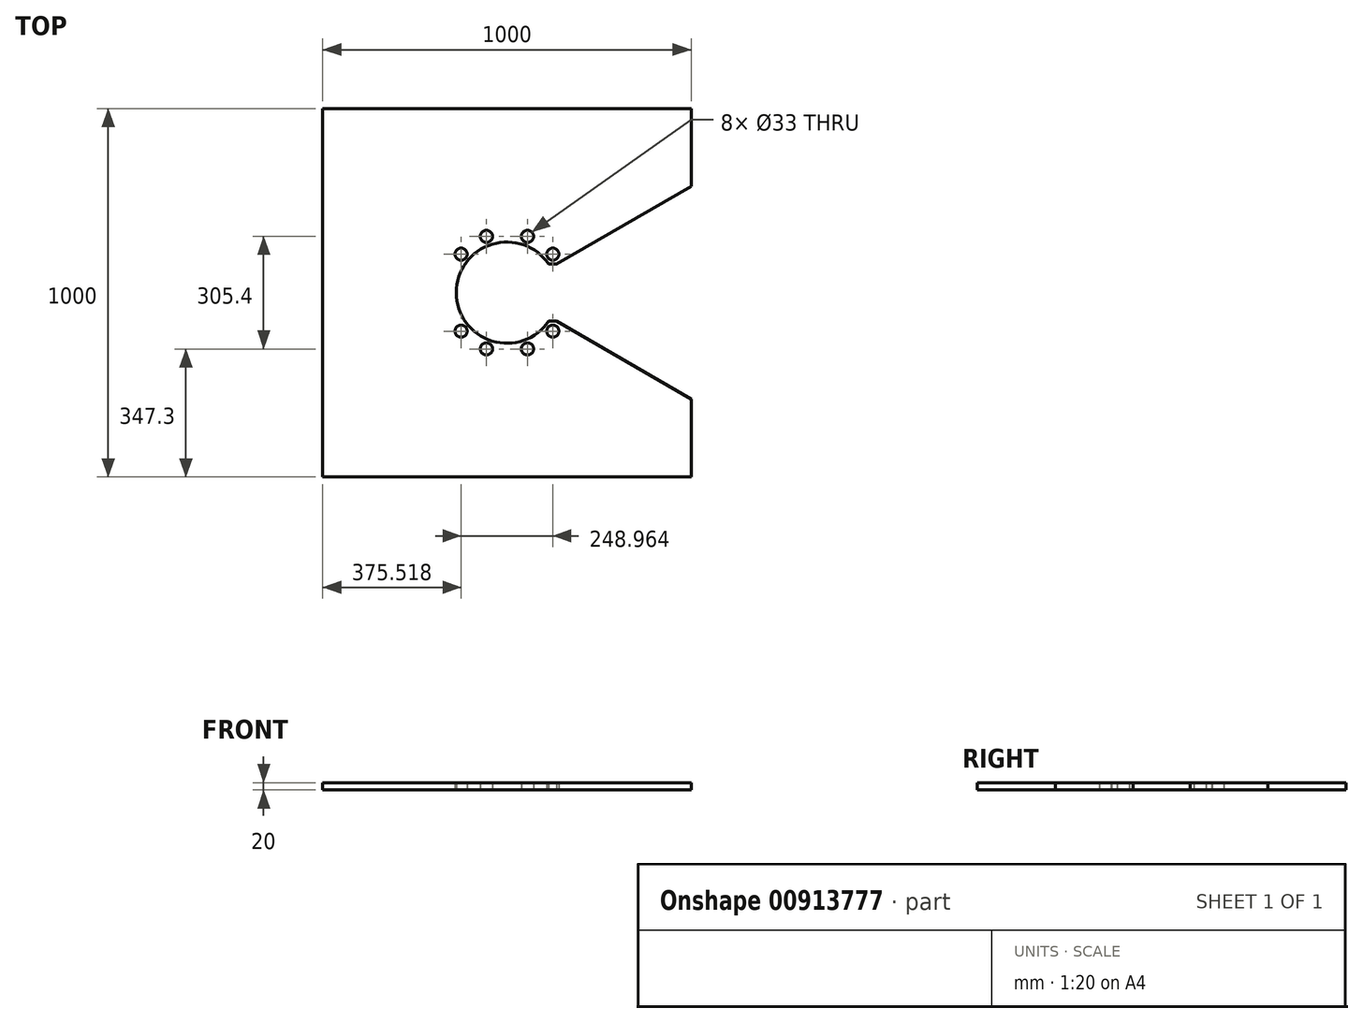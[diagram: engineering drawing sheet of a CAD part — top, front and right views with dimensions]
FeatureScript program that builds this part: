
annotation { "Feature Type Name" : "Feature", "Feature Type Description" : "" }
export const myFeature = defineFeature(function(context is Context, id is Id, definition is map)
    precondition{}
    {
        {
            var Q0;
            Q0=qCreatedBy(makeId("Top.planeOp"),FACE);
            var sketch = newSketch(context, id + "F0", { "sketchPlane" : qUnion([Q0])});
            skCircle(sketch, "E0", {"center": v(0, 0) * mm, "radius": 162.5 * mm, "construction": true});
            skLineSegment(sketch, "E1", {"start": v(0, 0) * mm, "end": v(72.3, 198.65) * mm, "construction": true});
            skCircle(sketch, "E2", {"center": v(55.58, 152.7) * mm, "radius": 16.5 * mm});
            skLineSegment(sketch, "E3", {"start": v(0, 0) * mm, "end": v(150.95, 126.66) * mm, "construction": true});
            skLineSegment(sketch, "E4", {"start": v(0, 0) * mm, "end": v(-63.14, 173.48) * mm, "construction": true});
            skLineSegment(sketch, "E5", {"start": v(0, 0) * mm, "end": v(-153.87, 129.1) * mm, "construction": true});
            skCircle(sketch, "E6", {"center": v(-55.58, 152.7) * mm, "radius": 16.5 * mm});
            skCircle(sketch, "E7", {"center": v(-124.48, 104.45) * mm, "radius": 16.5 * mm});
            skCircle(sketch, "E8", {"center": v(124.48, 104.45) * mm, "radius": 16.5 * mm});
            skCircle(sketch, "E9.MirrorC", {"center": v(-124.48, -104.45) * mm, "radius": 16.5 * mm});
            skCircle(sketch, "E10.MirrorC", {"center": v(-55.58, -152.7) * mm, "radius": 16.5 * mm});
            skCircle(sketch, "E11.MirrorC", {"center": v(55.58, -152.7) * mm, "radius": 16.5 * mm});
            skCircle(sketch, "E12.MirrorC", {"center": v(124.48, -104.45) * mm, "radius": 16.5 * mm});
            skArc(sketch, "E13", {"start": v(170.73, 77.5) * mm, "mid": v(-187.5, 0) * mm, "end": v(170.73, -77.5) * mm, "construction": true});
            skArc(sketch, "E14", {"start": v(113.58, 77.5) * mm, "mid": v(-137.5, 0) * mm, "end": v(113.58, -77.5) * mm});
            skCircle(sketch, "E15", {"center": v(0, 0) * mm, "radius": 77.5 * mm, "construction": true});
            skLineSegment(sketch, "E16.top", {"start": v(113.58, -77.5) * mm, "end": v(170.73, -77.5) * mm});
            skLineSegment(sketch, "E17.trimOffspring", {"start": v(113.58, 77.5) * mm, "end": v(170.73, 77.5) * mm});
            skLineSegment(sketch, "E18", {"start": v(0, 0) * mm, "end": v(648.68, 374.52) * mm});
            skLineSegment(sketch, "E19.MirrorCS", {"start": v(0, 0) * mm, "end": v(648.68, -374.52) * mm});
            skLineSegment(sketch, "E20.bottom", {"start": v(-500, 500) * mm, "end": v(500, 500) * mm});
            skLineSegment(sketch, "E20.top", {"start": v(-500, -500) * mm, "end": v(500, -500) * mm});
            skLineSegment(sketch, "E20.left", {"start": v(-500, 500) * mm, "end": v(-500, -500) * mm});
            skLineSegment(sketch, "E20.right", {"start": v(500, 500) * mm, "end": v(500, -500) * mm});
            skSolve(sketch);
        }
        {
            var Q0;
            Q0=makeQuery(id+"F0.imprint","IMPRINT",FACE,{"disambiguationData":[TD([[makeQuery(id+"F0.imprint","IMPRINT",EDGE,{"derivedFrom":sQuery(id+"F0.wireOp",EDGE,"E2")}),-1.0]])]});
            extrude(context, id + "F1", {"entities" : qUnion([Q0]), "depth" : 20 * mm, "offsetDistance" : 25 * mm});
        }
    });
